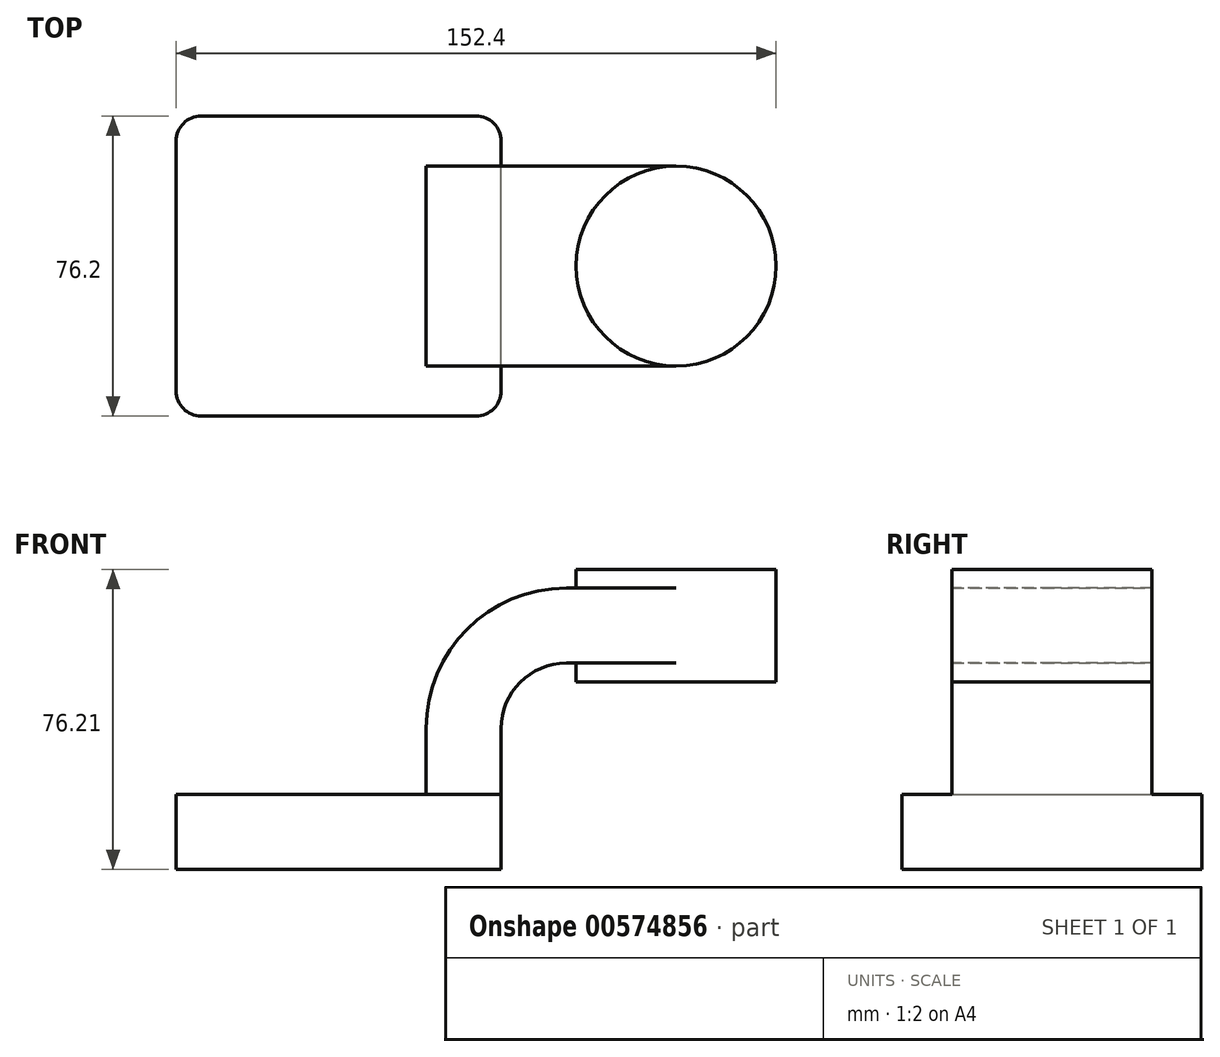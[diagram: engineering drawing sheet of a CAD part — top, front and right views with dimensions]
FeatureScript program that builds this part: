
annotation { "Feature Type Name" : "Feature", "Feature Type Description" : "" }
export const myFeature = defineFeature(function(context is Context, id is Id, definition is map)
    precondition{}
    {
        {
            var Q0;
            Q0=qCreatedBy(makeId("Front.planeOp"),FACE);
            var sketch = newSketch(context, id + "F0", { "sketchPlane" : qUnion([Q0])});
            skLineSegment(sketch, "E0.bottom", {"start": v(-41.28, -9.53) * mm, "end": v(41.28, -9.53) * mm});
            skLineSegment(sketch, "E0.top", {"start": v(-41.28, 9.53) * mm, "end": v(41.28, 9.53) * mm});
            skLineSegment(sketch, "E0.left", {"start": v(-41.28, -9.53) * mm, "end": v(-41.28, 9.53) * mm});
            skLineSegment(sketch, "E0.right", {"start": v(41.28, -9.53) * mm, "end": v(41.28, 9.53) * mm});
            skPoint(sketch, "E0.middle", {"position": v(0, 0) * mm});
            skLineSegment(sketch, "E1.bottom", {"start": v(60.33, 38.1) * mm, "end": v(111.13, 38.1) * mm});
            skLineSegment(sketch, "E1.top", {"start": v(60.33, 66.67) * mm, "end": v(111.13, 66.67) * mm});
            skLineSegment(sketch, "E1.left", {"start": v(60.33, 38.1) * mm, "end": v(60.33, 66.67) * mm});
            skLineSegment(sketch, "E1.right", {"start": v(111.13, 38.1) * mm, "end": v(111.13, 66.67) * mm});
            skPoint(sketch, "E1.middle", {"position": v(85.73, 52.39) * mm});
            skLineSegment(sketch, "E2", {"start": v(41.28, 9.52) * mm, "end": v(41.28, 26.31) * mm});
            skArc(sketch, "E3", {"start": v(41.28, 26.31) * mm, "mid": v(46.13, 38.02) * mm, "end": v(57.84, 42.88) * mm});
            skLineSegment(sketch, "E4", {"start": v(57.84, 42.88) * mm, "end": v(85.73, 42.88) * mm});
            skLineSegment(sketch, "E5.0", {"start": v(57.84, 61.93) * mm, "end": v(85.73, 61.93) * mm});
            skArc(sketch, "E5.1", {"start": v(22.23, 26.31) * mm, "mid": v(32.66, 51.5) * mm, "end": v(57.84, 61.93) * mm});
            skLineSegment(sketch, "E5.2", {"start": v(22.22, 9.52) * mm, "end": v(22.22, 26.31) * mm});
            skFitSpline(sketch, "E6", {"points": [v(-41.28, 9.52) * mm, v(57.84, 61.93) * mm], "startDerivative": vector(0, 66.34) * mm, "endDerivative": vector(150.28, 0) * mm});
            skPoint(sketch, "E7", {"position": v(71.78, 61.93) * mm});
            skLineSegment(sketch, "E8", {"start": v(85.73, 38.1) * mm, "end": v(85.73, 66.67) * mm});
            skSolve(sketch);
        }
        {
            var Q0;
            Q0=makeQuery(id+"F0.imprint","IMPRINT",FACE,{"disambiguationData":[TD([[makeQuery(id+"F0.imprint","IMPRINT",EDGE,{"derivedFrom":sQuery(id+"F0.wireOp",EDGE,"E0.bottom")}),1.0]])]});
            extrude(context, id + "F1", {"entities" : qUnion([Q0]), "endBound" : BoundingType.SYMMETRIC, "depth" : 76.2 * mm, "offsetDistance" : 25.4 * mm});
        }
        {
            var Q0;
            {var subQ1=sQuery(id+"F0.wireOp",EDGE,"E2");Q0=makeQuery(id+"F0.imprint","IMPRINT",FACE,{"disambiguationData":[TD([[makeQuery(id+"F0.imprint","IMPRINT",EDGE,{"derivedFrom":subQ1}),1.0]])]});}
            var Q1;
            {var subQ0=sQuery(id+"F0.wireOp",EDGE,"E4");var subQ1=sQuery(id+"F0.wireOp",EDGE,"E1.left");var subQ2=makeQuery(id+"F0.imprint","INTERSECT",VERTEX,{"derivedFrom":[subQ1,subQ0]});Q1=makeQuery(id+"F0.imprint","IMPRINT",FACE,{"disambiguationData":[TD([[makeQuery(id+"F0.imprint","IMPRINT",EDGE,{"disambiguationData":[TD([[subQ2,-1.0]])],"derivedFrom":subQ1}),-1.0]])]});}
            extrude(context, id + "F2", {"entities" : qUnion([Q0, Q1]), "operationType" : NewBodyOperationType.ADD, "endBound" : BoundingType.SYMMETRIC, "depth" : 50.8 * mm, "offsetDistance" : 25.4 * mm});
        }
        {
            var Q0;
            Q0=makeQuery(id+"F0.imprint","IMPRINT",FACE,{"disambiguationData":[TD([[makeQuery(id+"F0.imprint","IMPRINT",EDGE,{"derivedFrom":sQuery(id+"F0.wireOp",EDGE,"E5.1")}),1.0]])]});
            extrude(context, id + "F3", {"entities" : qUnion([Q0]), "operationType" : NewBodyOperationType.ADD, "endBound" : BoundingType.SYMMETRIC, "depth" : 15.88 * mm, "offsetDistance" : 25.4 * mm});
        }
        {
            var Q0;
            {var subQ4=sQuery(id+"F0.wireOp",EDGE,"E1.right");Q0=makeQuery(id+"F0.imprint","IMPRINT",FACE,{"disambiguationData":[TD([[makeQuery(id+"F0.imprint","IMPRINT",EDGE,{"derivedFrom":subQ4}),1.0]])]});}
            var Q1;
            Q1=sQuery(id+"F0.wireOp",EDGE,"E8");
            revolve(context, id + "F4", {"operationType" : NewBodyOperationType.ADD, "entities" : qUnion([Q0]), "axis" : qUnion([Q1]), "revolveType" : RevolveType.FULL});
        }
        {
            var Q0;
            Q0=makeQuery(id+"F1.opExtrude","CAP_EDGE",EDGE,{"disambiguationData":[OSD([sQuery(id+"F0.wireOp",EDGE,"E0.left")])],"isStart":false});
            var Q1;
            Q1=makeQuery(id+"F1.opExtrude","CAP_EDGE",EDGE,{"disambiguationData":[OSD([sQuery(id+"F0.wireOp",EDGE,"E0.right")])],"isStart":false});
            var Q2;
            Q2=makeQuery(id+"F1.opExtrude","CAP_EDGE",EDGE,{"disambiguationData":[OSD([sQuery(id+"F0.wireOp",EDGE,"E0.right")])],"isStart":true});
            var Q3;
            Q3=makeQuery(id+"F1.opExtrude","CAP_EDGE",EDGE,{"disambiguationData":[OSD([sQuery(id+"F0.wireOp",EDGE,"E0.left")])],"isStart":true});
            fillet(context, id + "F5", {"entities" : qUnion([Q0, Q1, Q2, Q3]), "radius" : 6.35 * mm, "tangentPropagation" : true, "allowEdgeOverflow" : false});
        }
    });
